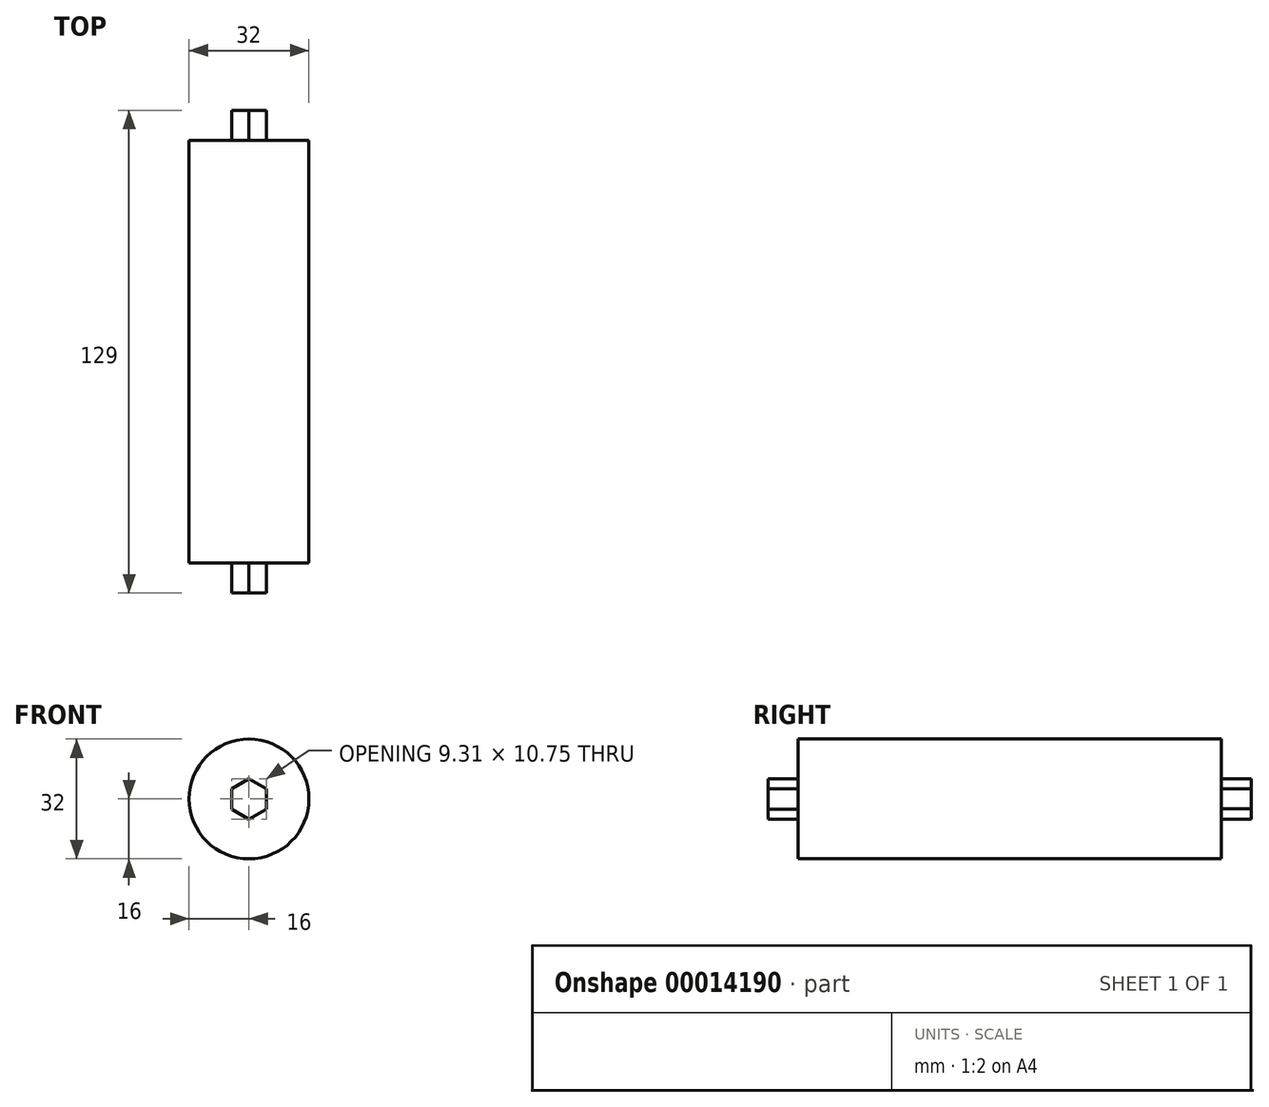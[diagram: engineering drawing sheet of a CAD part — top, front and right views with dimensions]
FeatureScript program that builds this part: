
annotation { "Feature Type Name" : "Feature", "Feature Type Description" : "" }
export const myFeature = defineFeature(function(context is Context, id is Id, definition is map)
    precondition{}
    {
        {
            var Q0;
            Q0=qCreatedBy(makeId("Front.planeOp"),FACE);
            var sketch = newSketch(context, id + "F0", { "sketchPlane" : qUnion([Q0])});
            skCircle(sketch, "E0", {"center": v(0, 0) * mm, "radius": 16 * mm});
            skSolve(sketch);
        }
        {
            var Q0;
            Q0 = qSketchRegion(id + "F0", true);
            extrude(context, id + "F1", {"entities" : qUnion([Q0]), "depth" : 113 * mm});
        }
        {
            var Q0;
            Q0=makeQuery(id+"F1.opExtrude","CAP_FACE",FACE,{"disambiguationData":[OSD([sQuery(id+"F0.wireOp",EDGE,"E0")])],"isStart":false});
            var sketch = newSketch(context, id + "F2", { "sketchPlane" : qUnion([Q0])});
            skCircle(sketch, "E1.cCircle", {"center": v(0, 0) * mm, "radius": 4.65 * mm, "construction": true});
            skLineSegment(sketch, "E1.0", {"start": v(4.65, 2.69) * mm, "end": v(4.65, -2.69) * mm});
            skLineSegment(sketch, "E1.1", {"start": v(4.65, -2.69) * mm, "end": v(0, -5.37) * mm});
            skLineSegment(sketch, "E1.2", {"start": v(0, -5.37) * mm, "end": v(-4.65, -2.69) * mm});
            skLineSegment(sketch, "E1.3", {"start": v(-4.65, -2.69) * mm, "end": v(-4.65, 2.69) * mm});
            skLineSegment(sketch, "E1.4", {"start": v(-4.65, 2.69) * mm, "end": v(0, 5.37) * mm});
            skLineSegment(sketch, "E1.5", {"start": v(0, 5.37) * mm, "end": v(4.65, 2.69) * mm});
            skPoint(sketch, "E1.0.midPoint", {"position": v(4.65, 0) * mm});
            skSolve(sketch);
        }
        {
            var Q0;
            Q0 = qSketchRegion(id + "F2", true);
            extrude(context, id + "F3", {"entities" : qUnion([Q0]), "operationType" : NewBodyOperationType.ADD, "depth" : 8 * mm});
        }
        {
            var Q0;
            Q0=makeQuery(id+"F1.opExtrude","CAP_FACE",FACE,{"disambiguationData":[OSD([sQuery(id+"F0.wireOp",EDGE,"E0")])],"isStart":true});
            var sketch = newSketch(context, id + "F4", { "sketchPlane" : qUnion([Q0])});
            skPoint(sketch, "E2.0.midPoint", {"position": v(4.65, 0.01) * mm});
            skCircle(sketch, "E2.cCircle", {"center": v(0, 0.01) * mm, "radius": 4.65 * mm, "construction": true});
            skLineSegment(sketch, "E2.0", {"start": v(4.65, 2.7) * mm, "end": v(4.65, -2.68) * mm});
            skLineSegment(sketch, "E2.1", {"start": v(4.65, -2.68) * mm, "end": v(0, -5.36) * mm});
            skLineSegment(sketch, "E2.2", {"start": v(0, -5.36) * mm, "end": v(-4.65, -2.68) * mm});
            skLineSegment(sketch, "E2.3", {"start": v(-4.65, -2.68) * mm, "end": v(-4.65, 2.7) * mm});
            skLineSegment(sketch, "E2.4", {"start": v(-4.65, 2.7) * mm, "end": v(0, 5.39) * mm});
            skLineSegment(sketch, "E2.5", {"start": v(0, 5.39) * mm, "end": v(4.65, 2.7) * mm});
            skSolve(sketch);
        }
        {
            var Q0;
            Q0 = qSketchRegion(id + "F4", true);
            extrude(context, id + "F5", {"entities" : qUnion([Q0]), "operationType" : NewBodyOperationType.ADD, "depth" : 8 * mm});
        }
    });
